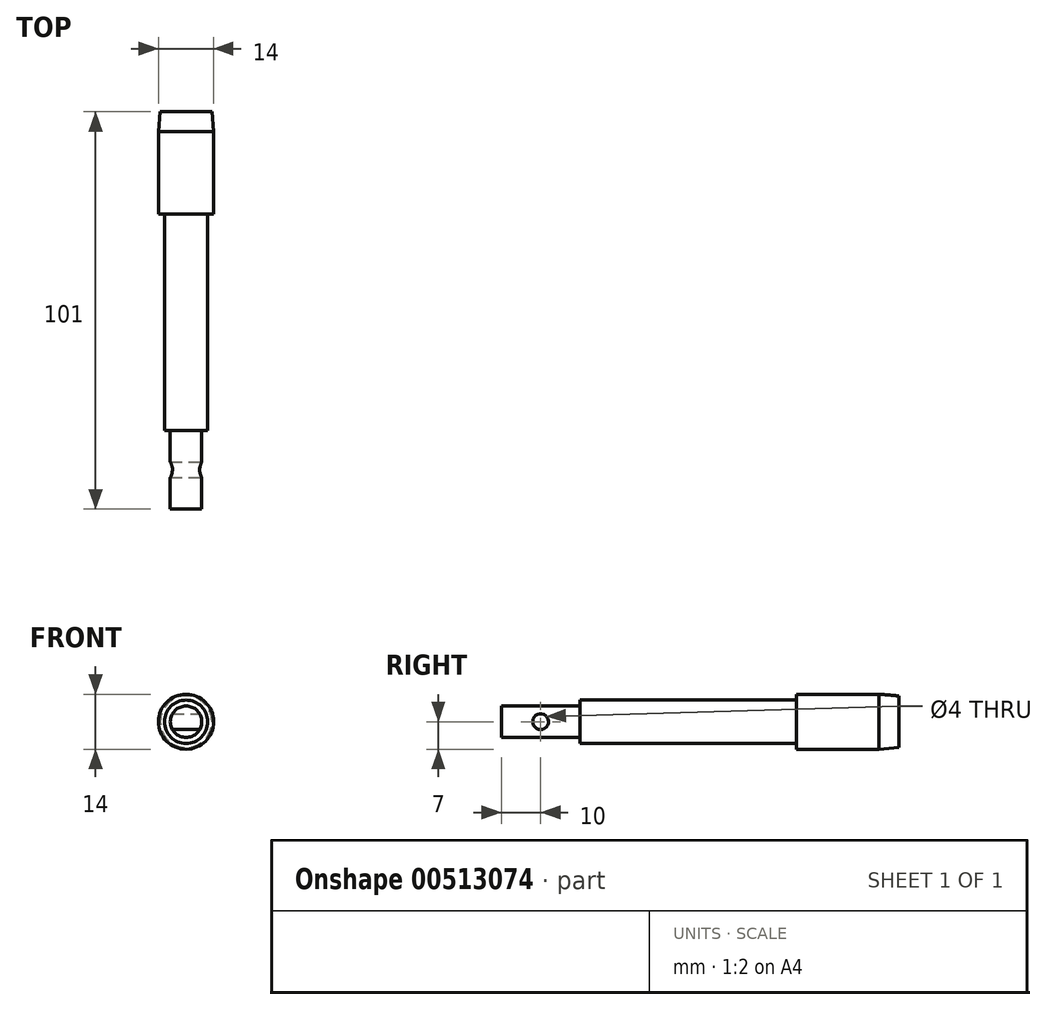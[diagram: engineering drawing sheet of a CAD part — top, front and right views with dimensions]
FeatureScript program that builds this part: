
annotation { "Feature Type Name" : "Feature", "Feature Type Description" : "" }
export const myFeature = defineFeature(function(context is Context, id is Id, definition is map)
    precondition{}
    {
        {
            var Q0;
            Q0=qCreatedBy(makeId("Front.planeOp"),FACE);
            var sketch = newSketch(context, id + "F0", { "sketchPlane" : qUnion([Q0])});
            skCircle(sketch, "E0", {"center": v(0, 0) * mm, "radius": 5.5 * mm});
            skSolve(sketch);
        }
        {
            var Q0;
            Q0=qSketchRegion(id+"F0",true);
            extrude(context, id + "F1", {"entities" : qUnion([Q0]), "depth" : 75 * mm});
        }
        {
            var Q0;
            Q0=makeQuery(id+"F1.opExtrude","CAP_FACE",FACE,{"disambiguationData":[OSD([sQuery(id+"F0.wireOp",EDGE,"E0")])],"isStart":true});
            var sketch = newSketch(context, id + "F2", { "sketchPlane" : qUnion([Q0])});
            skCircle(sketch, "E1", {"center": v(0, 0) * mm, "radius": 7 * mm});
            skSolve(sketch);
        }
        {
            var Q0;
            Q0=qSketchRegion(id+"F2",true);
            extrude(context, id + "F3", {"entities" : qUnion([Q0]), "operationType" : NewBodyOperationType.ADD, "depth" : 26 * mm});
        }
        {
            var Q0;
            Q0=makeQuery(id+"F3.opExtrude","CAP_EDGE",EDGE,{"disambiguationData":[OSD([sQuery(id+"F2.wireOp",EDGE,"E1")])],"isStart":false});
            chamfer(context, id + "F4", {"entities" : qUnion([Q0]), "chamferType" : ChamferType.OFFSET_ANGLE, "width" : 5 * mm, "oppositeDirection" : true, "angle" : 5 * degree, "tangentPropagation" : true});
        }
        {
            var Q0;
            Q0=makeQuery(id+"F1.opExtrude","CAP_FACE",FACE,{"disambiguationData":[OSD([sQuery(id+"F0.wireOp",EDGE,"E0")])],"isStart":false});
            var sketch = newSketch(context, id + "F5", { "sketchPlane" : qUnion([Q0])});
            skCircle(sketch, "E2", {"center": v(0, 0) * mm, "radius": 4 * mm});
            skSolve(sketch);
        }
        {
            var Q0;
            Q0=makeQuery(id+"F5.imprint","IMPRINT",FACE,{"disambiguationData":[TD([[makeQuery(id+"F5.imprint","IMPRINT",EDGE,{"derivedFrom":sQuery(id+"F5.wireOp",EDGE,"E2")}),-1.0]])]});
            extrude(context, id + "F6", {"entities" : qUnion([Q0]), "operationType" : NewBodyOperationType.REMOVE, "oppositeDirection" : true, "depth" : 20 * mm});
        }
        {
            var Q0;
            Q0=qCreatedBy(makeId("Right.planeOp"),FACE);
            var sketch = newSketch(context, id + "F7", { "sketchPlane" : qUnion([Q0])});
            skCircle(sketch, "E3", {"center": v(-65, 0) * mm, "radius": 2 * mm});
            skSolve(sketch);
        }
        {
            var Q0;
            Q0 = qSketchRegion(id + "F7", true);
            extrude(context, id + "F8", {"entities" : qUnion([Q0]), "operationType" : NewBodyOperationType.REMOVE, "endBound" : BoundingType.SYMMETRIC, "oppositeDirection" : true, "depth" : 25 * mm});
        }
    });
